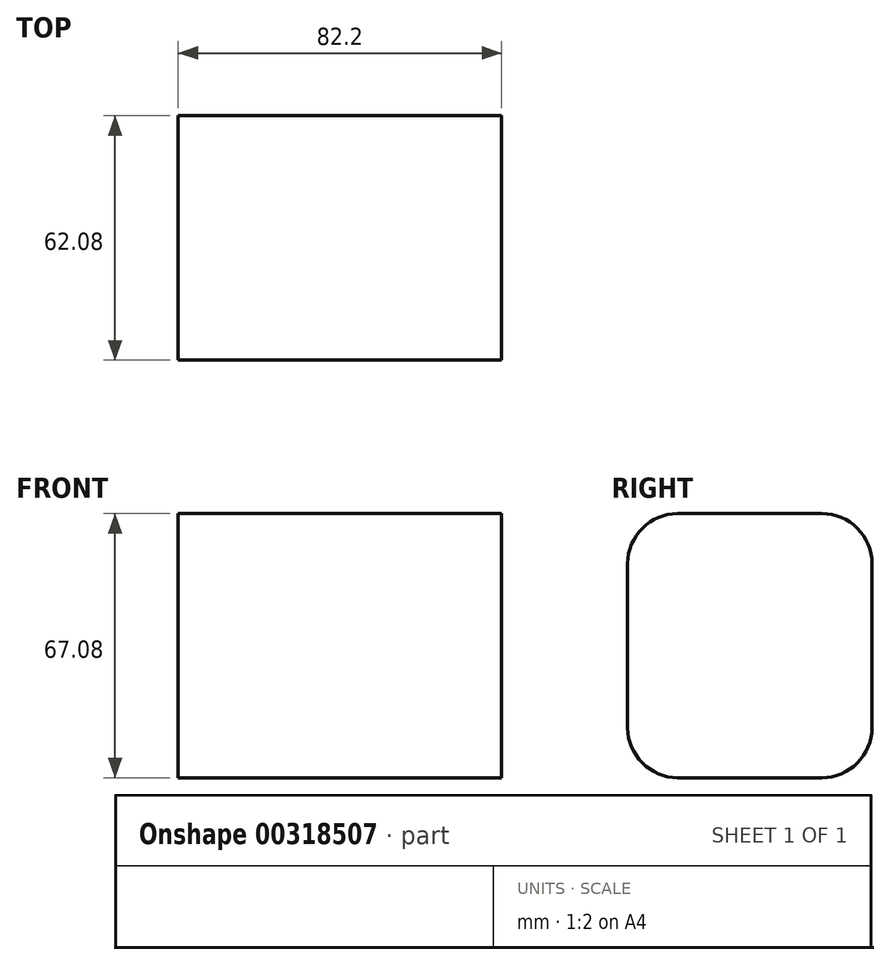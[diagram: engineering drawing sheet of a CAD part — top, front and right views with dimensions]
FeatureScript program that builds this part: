
annotation { "Feature Type Name" : "Feature", "Feature Type Description" : "" }
export const myFeature = defineFeature(function(context is Context, id is Id, definition is map)
    precondition{}
    {
        {
            var Q0;
            Q0=qCreatedBy(makeId("Front.planeOp"),FACE);
            var sketch = newSketch(context, id + "F0", { "sketchPlane" : qUnion([Q0])});
            skLineSegment(sketch, "E0.bottom", {"start": v(-41.1, 33.54) * mm, "end": v(41.1, 33.54) * mm});
            skLineSegment(sketch, "E0.top", {"start": v(-41.1, -33.54) * mm, "end": v(41.1, -33.54) * mm});
            skLineSegment(sketch, "E0.left", {"start": v(-41.1, 33.54) * mm, "end": v(-41.1, -33.54) * mm});
            skLineSegment(sketch, "E0.right", {"start": v(41.1, 33.54) * mm, "end": v(41.1, -33.54) * mm});
            skPoint(sketch, "E0.middle", {"position": v(0, 0) * mm});
            skSolve(sketch);
        }
        {
            var Q0;
            Q0=makeQuery(id+"F0.imprint","IMPRINT",FACE,{"disambiguationData":[TD([[makeQuery(id+"F0.imprint","IMPRINT",EDGE,{"derivedFrom":sQuery(id+"F0.wireOp",EDGE,"E0.bottom")}),-1.0]])]});
            extrude(context, id + "F1", {"entities" : qUnion([Q0]), "depth" : 62.08 * mm});
        }
        {
            var Q0;
            Q0=makeQuery(id+"F1.opExtrude","CAP_EDGE",EDGE,{"disambiguationData":[OSD([sQuery(id+"F0.wireOp",EDGE,"E0.bottom")])],"isStart":false});
            fillet(context, id + "F2", {"entities" : qUnion([Q0]), "radius" : 12.7 * mm, "tangentPropagation" : true, "allowEdgeOverflow" : false});
        }
        {
            var Q0;
            Q0=makeQuery(id+"F1.opExtrude","CAP_EDGE",EDGE,{"disambiguationData":[OSD([sQuery(id+"F0.wireOp",EDGE,"E0.top")])],"isStart":false});
            fillet(context, id + "F3", {"entities" : qUnion([Q0]), "radius" : 12.7 * mm, "tangentPropagation" : true, "allowEdgeOverflow" : false});
        }
        {
            var Q0;
            Q0=makeQuery(id+"F1.opExtrude","CAP_EDGE",EDGE,{"disambiguationData":[OSD([sQuery(id+"F0.wireOp",EDGE,"E0.top")])],"isStart":true});
            var Q1;
            Q1=makeQuery(id+"F1.opExtrude","CAP_EDGE",EDGE,{"disambiguationData":[OSD([sQuery(id+"F0.wireOp",EDGE,"E0.bottom")])],"isStart":true});
            fillet(context, id + "F4", {"entities" : qUnion([Q0, Q1]), "radius" : 12.7 * mm, "tangentPropagation" : true, "allowEdgeOverflow" : false});
        }
    });
